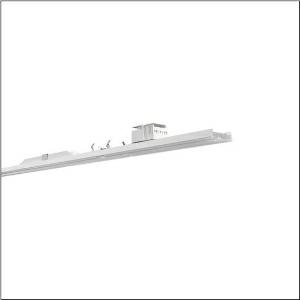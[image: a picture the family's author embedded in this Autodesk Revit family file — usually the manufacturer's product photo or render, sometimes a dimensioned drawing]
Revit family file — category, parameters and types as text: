
# Revit family: licross_r__11_recessed_ho_51tl12dn4dxld_2425
name_source: partatom
category: Lighting Fixtures
units: mm (PartAtom-declared; Revit-internal decimal feet)

## family parameters
Cut with Voids When Loaded = No
Host = Face
Light Source = No
Part Type = Normal
Room Calculation Point = No
Round Connector Dimension = Use Diameter
Shared = No

## types (1)
- --- (1 x LED, 2020 lm, 13 W, 4000K)
    Apparent Load = 13 VA
    CIE Flux Codes = 66 91 98 100 100
    Color Rendering = 80
    Color Temperature = 4000K
    Default Elevation = 1800 mm
    Description = Licross® 11 Recessed HOluminaire insert, length: 1.500mm, width: 66mm, height: 67mm, LED rated luminous flux: 13.000lm, light colour: 840, control gear: DALI 2, control gear: ECG DALI, with plug, 6-pole, with phase selection, mains connection: 220..240V, AC/DC, 0/50..60Hz, without changeover relay, for emergency light function, for central battery installations according to DIN EN 60598-2-22, halogen-free wiring, primary optical cover: cover, of PMMA, light emission: direct distribution, protection rating (complete): IP40, insulation class (complete): insulation class I (protective earthing), certification: CE, ENEC, VDE, protection symbol: D if used in an environment without relevant dust loads with corresponding accessories, permissible ambient temperature for indoor applications: -25..+35°C, standard: EN 60598-2-22, reducing of maximum allowable ambient temperature of 5°C with ceiling mounting, corresponds to IFS (International Featured Standards) requirements for safety and quality in the food industry, packaging unit: 1 piece
    Height = 58 mm
    Lamp = 1 x LED
    Lamp Light Flux = 2020 lm
    Lamp Power = 13 W
    Lamp count = 1
    Length = 1500 mm
    Luminous efficacy = 155 lm/W
    Manufacturer = Siteco
    ModVariant = No
    Model = 51TL12DN4DXLD
    Mounting Place = Ceiling
    Mounting Type = Pendant
    Number of Poles = 1
    OnlyDefault = Yes
    Power Factor = 1
    Product Name = Licross® 11 Recessed HO
    Product group = luminaire insert
    ProductGroupID = 902
    Protection Class = Protection class I
    Protection Degree = IP 40
    RLX_Detail_Level = 1
    RlxData = <blob elided: 22705 chars, md5=eb97ccd0>
    Socket = socket
    Standby Power = 0 W
    System Light Flux = 2020 lm
    System Power = 13 W
    Type Comments = : DC mode (central or group accumulator) initial emergency light level
    Type Image = l_1266722.jpg
    URL = http://relux.com
    VarID = @adj_134289
    Voltage = 0 V
    Weight = 0.00 kg
    Width = 66 mm

## geometry (parser evidence)
native form markers: Blend x4, Sweep x11
no freeform markers — native parametric forms only
